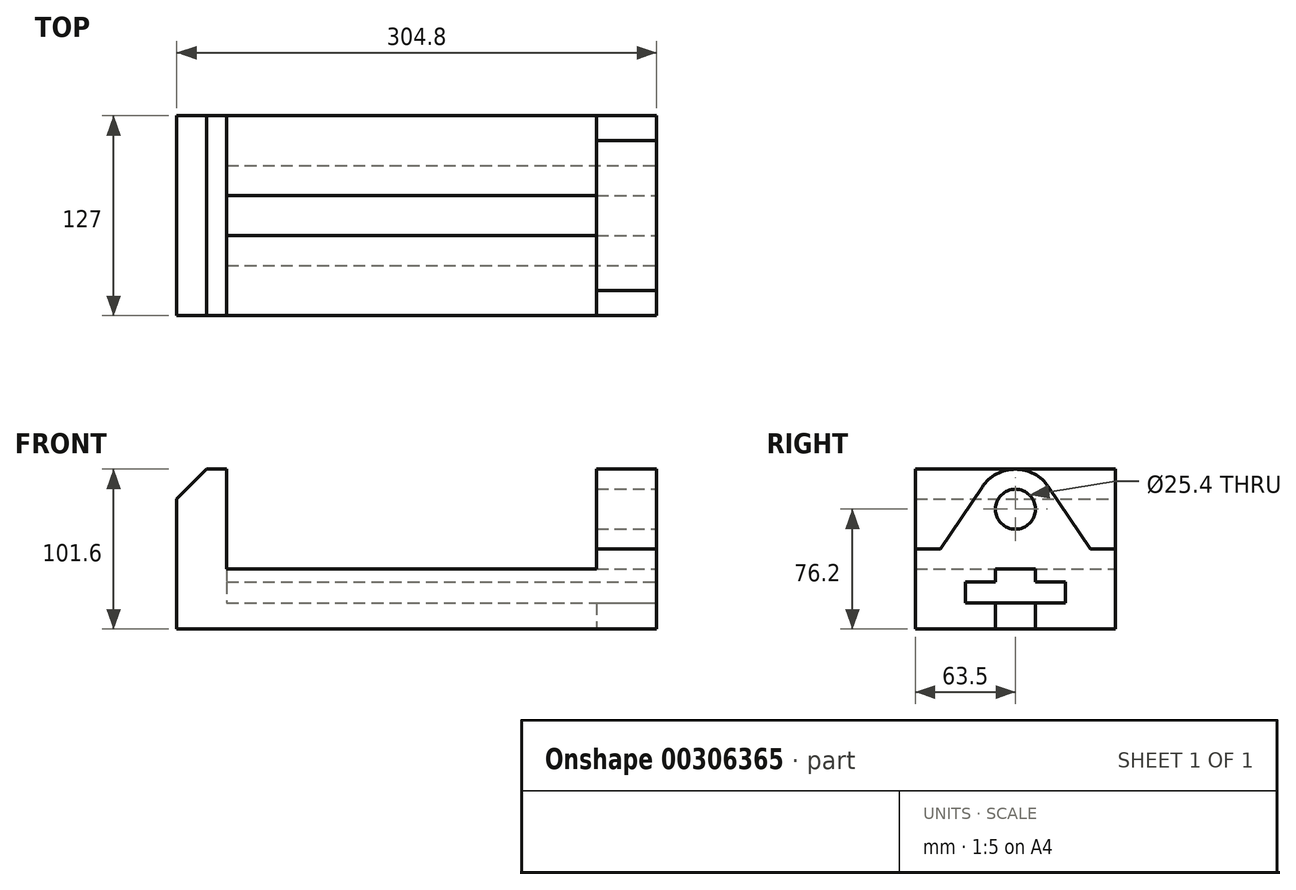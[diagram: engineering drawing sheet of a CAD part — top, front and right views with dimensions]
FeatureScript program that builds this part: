
annotation { "Feature Type Name" : "Feature", "Feature Type Description" : "" }
export const myFeature = defineFeature(function(context is Context, id is Id, definition is map)
    precondition{}
    {
        {
            var Q0;
            Q0=qCreatedBy(makeId("Front.planeOp"),FACE);
            var sketch = newSketch(context, id + "F0", { "sketchPlane" : qUnion([Q0])});
            skLineSegment(sketch, "E0.bottom", {"start": v(0, 0) * mm, "end": v(304.8, 0) * mm});
            skLineSegment(sketch, "E0.top", {"start": v(19.05, 101.6) * mm, "end": v(31.75, 101.6) * mm});
            skLineSegment(sketch, "E0.left", {"start": v(0, 0) * mm, "end": v(0, 82.55) * mm});
            skLineSegment(sketch, "E0.right", {"start": v(304.8, 0) * mm, "end": v(304.8, 101.6) * mm});
            skLineSegment(sketch, "E1", {"start": v(31.75, 38.1) * mm, "end": v(31.75, 101.6) * mm});
            skLineSegment(sketch, "E2", {"start": v(266.7, 38.1) * mm, "end": v(31.75, 38.1) * mm});
            skLineSegment(sketch, "E3.trimOffspring", {"start": v(266.7, 101.6) * mm, "end": v(304.8, 101.6) * mm});
            skLineSegment(sketch, "E4", {"start": v(266.7, 101.6) * mm, "end": v(266.7, 38.1) * mm});
            skLineSegment(sketch, "E5", {"start": v(304.8, 50.8) * mm, "end": v(266.7, 50.8) * mm});
            skLineSegment(sketch, "E6", {"start": v(19.05, 101.6) * mm, "end": v(0, 82.55) * mm});
            skSolve(sketch);
        }
        {
            var Q0;
            Q0 = qSketchRegion(id + "F0", true);
            extrude(context, id + "F1", {"entities" : qUnion([Q0]), "depth" : 127 * mm});
        }
        {
            var Q0;
            Q0=makeQuery(id+"F1.opExtrude","SWEPT_FACE",FACE,{"disambiguationData":[OSD([sQuery(id+"F0.wireOp",EDGE,"E0.right")])]});
            var sketch = newSketch(context, id + "F2", { "sketchPlane" : qUnion([Q0])});
            skLineSegment(sketch, "E7.bottom", {"start": v(-50.8, 38.1) * mm, "end": v(-76.2, 38.1) * mm});
            skLineSegment(sketch, "E8", {"start": v(-76.2, 38.1) * mm, "end": v(-76.2, 29.84) * mm});
            skLineSegment(sketch, "E9", {"start": v(-76.2, 29.84) * mm, "end": v(-95.25, 29.84) * mm});
            skLineSegment(sketch, "E10", {"start": v(-95.25, 29.84) * mm, "end": v(-95.25, 16.5) * mm});
            skLineSegment(sketch, "E11", {"start": v(-95.25, 16.5) * mm, "end": v(-76.2, 16.5) * mm});
            skLineSegment(sketch, "E12.trimOffspring", {"start": v(-76.2, 16.5) * mm, "end": v(-76.2, 0) * mm});
            skLineSegment(sketch, "E13", {"start": v(-76.2, 29.84) * mm, "end": v(-50.8, 29.84) * mm});
            skLineSegment(sketch, "E14", {"start": v(-50.8, 29.84) * mm, "end": v(-50.8, 38.1) * mm});
            skLineSegment(sketch, "E15", {"start": v(-50.8, 29.84) * mm, "end": v(-31.75, 29.84) * mm});
            skLineSegment(sketch, "E16", {"start": v(-31.75, 29.84) * mm, "end": v(-31.75, 16.5) * mm});
            skLineSegment(sketch, "E17", {"start": v(-31.75, 16.5) * mm, "end": v(-50.8, 16.5) * mm});
            skLineSegment(sketch, "E18", {"start": v(-50.8, 16.5) * mm, "end": v(-50.8, 0) * mm});
            skLineSegment(sketch, "E19", {"start": v(-76.2, 16.5) * mm, "end": v(-50.8, 16.5) * mm});
            skSolve(sketch);
        }
        {
            var Q0;
            Q0 = qSketchRegion(id + "F2", true);
            var Q1;
            Q1=makeQuery(id+"F2.imprint","IMPRINT",FACE,{"disambiguationData":[TD([[makeQuery(id+"F2.imprint","IMPRINT",EDGE,{"derivedFrom":sQuery(id+"F2.wireOp",EDGE,"E7.bottom")}),1.0]])]});
            extrude(context, id + "F3", {"entities" : qUnion([Q0, Q1]), "operationType" : NewBodyOperationType.REMOVE, "oppositeDirection" : true, "depth" : 273.05 * mm});
        }
        {
            var Q0;
            Q0=makeQuery(id+"F1.opExtrude","SWEPT_FACE",FACE,{"disambiguationData":[OSD([sQuery(id+"F0.wireOp",EDGE,"E0.right")])]});
            var sketch = newSketch(context, id + "F4", { "sketchPlane" : qUnion([Q0])});
            skLineSegment(sketch, "E20", {"start": v(-127, 50.8) * mm, "end": v(-111.12, 50.8) * mm});
            skPoint(sketch, "E21", {"position": v(-111.12, 50.8) * mm});
            skPoint(sketch, "E22", {"position": v(-15.87, 50.8) * mm});
            skLineSegment(sketch, "E23.trimOffspring", {"start": v(-15.87, 50.8) * mm, "end": v(0, 50.8) * mm});
            skPoint(sketch, "E24.positionSnap0", {"position": v(-63.5, 101.6) * mm});
            skCircle(sketch, "E25", {"center": v(-63.5, 76.2) * mm, "radius": 12.7 * mm});
            skArc(sketch, "E26", {"start": v(-42.4, 90.35) * mm, "mid": v(-63.5, 101.6) * mm, "end": v(-84.6, 90.35) * mm});
            skLineSegment(sketch, "E27", {"start": v(-111.12, 50.8) * mm, "end": v(-84.6, 90.35) * mm});
            skLineSegment(sketch, "E28", {"start": v(-15.87, 50.8) * mm, "end": v(-42.4, 90.35) * mm});
            skSolve(sketch);
        }
        {
            var Q0;
            {var subQ7=sQuery(id+"F4.wireOp",EDGE,"E23.trimOffspring");Q0=makeQuery(id+"F4.imprint","IMPRINT",FACE,{"disambiguationData":[TD([[makeQuery(id+"F4.imprint","IMPRINT",EDGE,{"derivedFrom":subQ7}),1.0]])]});}
            var Q1;
            {var subQ7=sQuery(id+"F4.wireOp",EDGE,"E20");Q1=makeQuery(id+"F4.imprint","IMPRINT",FACE,{"disambiguationData":[TD([[makeQuery(id+"F4.imprint","IMPRINT",EDGE,{"derivedFrom":subQ7}),1.0]])]});}
            extrude(context, id + "F5", {"entities" : qUnion([Q0, Q1]), "operationType" : NewBodyOperationType.REMOVE, "endBound" : BoundingType.UP_TO_NEXT, "oppositeDirection" : true, "depth" : 25.4 * mm});
        }
        {
            var Q0;
            Q0=makeQuery(id+"F4.imprint","IMPRINT",FACE,{"disambiguationData":[TD([[makeQuery(id+"F4.imprint","IMPRINT",EDGE,{"derivedFrom":sQuery(id+"F4.wireOp",EDGE,"E25")}),1.0]])]});
            extrude(context, id + "F6", {"entities" : qUnion([Q0]), "operationType" : NewBodyOperationType.REMOVE, "endBound" : BoundingType.UP_TO_NEXT, "oppositeDirection" : true, "depth" : 25.4 * mm});
        }
        {
            var Q0;
            {var subQ0=sQuery(id+"F2.wireOp",EDGE,"E12.trimOffspring");Q0=makeQuery(id+"F2.imprint","IMPRINT",FACE,{"disambiguationData":[TD([[makeQuery(id+"F2.imprint","IMPRINT",EDGE,{"derivedFrom":subQ0}),1.0]])]});}
            extrude(context, id + "F7", {"entities" : qUnion([Q0]), "operationType" : NewBodyOperationType.REMOVE, "oppositeDirection" : true, "depth" : 38.1 * mm});
        }
    });
